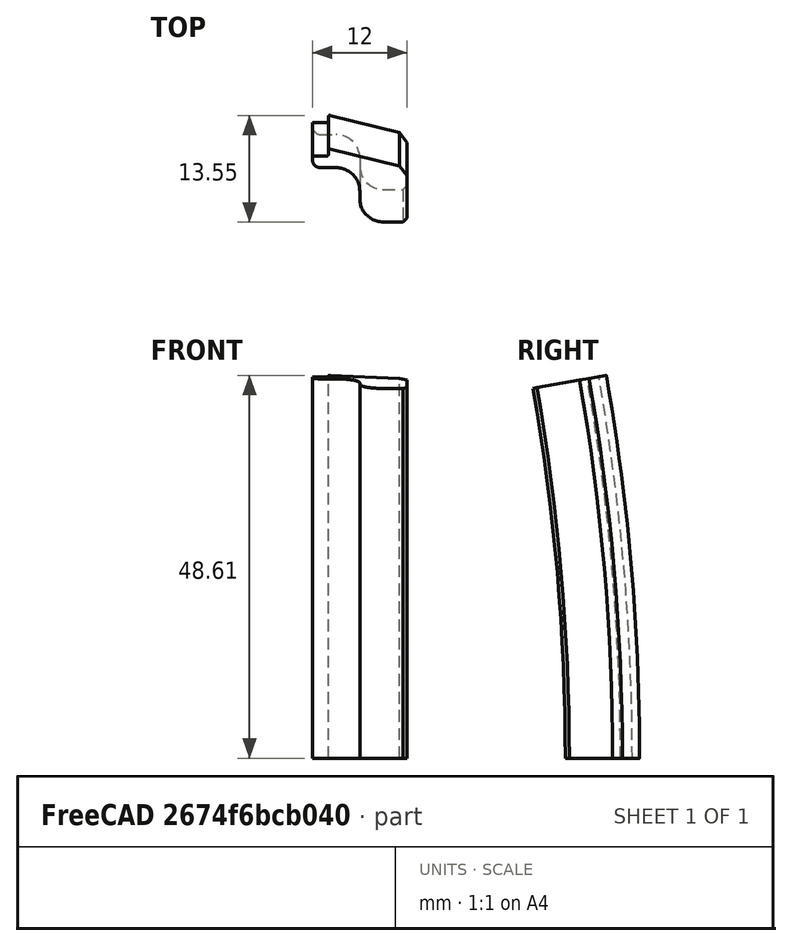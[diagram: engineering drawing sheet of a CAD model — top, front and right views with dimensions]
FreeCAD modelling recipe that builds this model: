
FCSTD DOCUMENT  (FreeCAD 0.16R)
Label: BeadLock3
License: All rights reserved
LicenseURL: http://en.wikipedia.org/wiki/All_rights_reserved
objects: PartDesign::Fillet×5, PartDesign::Chamfer×2, Sketcher::SketchObject×1, PartDesign::Revolution×1, Mesh::Feature×1
note: 10 computed .brp shape members not serialized (recipe doc carries the construction recipe); baked Part::Feature solids carry a one-line shape summary decoded from their .brp

FEATURE [Sketcher::SketchObject] Sketch
  sketch-geometry (8):
    g0: LineSegment StartX=0 StartY=279 StartZ=0 EndX=2 EndY=279 EndZ=0
    g1: LineSegment StartX=2 StartY=279 StartZ=0 EndX=2 EndY=280 EndZ=0
    g2: LineSegment StartX=0 StartY=277.5 StartZ=0 EndX=0 EndY=279 EndZ=0
    g3: LineSegment StartX=0 StartY=277.5 StartZ=0 EndX=6 EndY=277.5 EndZ=0
    g4: LineSegment StartX=6 StartY=277.5 StartZ=0 EndX=6 EndY=270.5 EndZ=0
    g5: LineSegment StartX=6 StartY=270.5 StartZ=0 EndX=12 EndY=270.5 EndZ=0
    g6: LineSegment StartX=12 StartY=270.5 StartZ=0 EndX=12 EndY=277.5 EndZ=0
    g7: LineSegment StartX=2 StartY=280 StartZ=0 EndX=12 EndY=277.5 EndZ=0
  constraints (24):
    c: Horizontal(g0)
    c: PointOnObject(g0,g-2)
    c: DistanceY(g0) = 279
    c: Distance(g0) = 2
    c: Coincident(g1,g0)
    c: Vertical(g1)
    c: Distance(g1) = 1
    c: Vertical(g2)
    c: Coincident(g2,g0)
    c: Distance(g2) = 1.5
    c: Horizontal(g3)
    c: Coincident(g3,g2)
    c: Distance(g3) = 6
    c: Vertical(g4)
    c: Coincident(g4,g3)
    c: Distance(g4) = 7
    c: Horizontal(g5)
    c: Coincident(g5,g4)
    c: Distance(g5) = 6
    c: Vertical(g6)
    c: Coincident(g5,g6)
    c: Distance(g6) = 7
    c: Coincident(g7,g1)
    c: Coincident(g7,g6)
FEATURE [PartDesign::Revolution] Revolution
  Angle = 10
  Axis = (1,0,0)
  Base = (0,0,0)
  ReferenceAxis = -> Sketch [H_Axis]
  Sketch = -> Sketch
FEATURE [PartDesign::Fillet] Fillet
  Base = -> Revolution [Edge17]
  Radius = 3
FEATURE [PartDesign::Fillet] Fillet001
  Base = -> Fillet [Edge23]
  Radius = 1
FEATURE [PartDesign::Fillet] Fillet002
  Base = -> Fillet001 [Edge26]
  Radius = 0.2
FEATURE [PartDesign::Fillet] Fillet003
  Base = -> Fillet002 [Edge13]
  Radius = 0.2
FEATURE [PartDesign::Chamfer] Chamfer
  Base = -> Fillet003 [Edge22]
  Size = 1
FEATURE [PartDesign::Chamfer] Chamfer001
  Base = -> Chamfer [Edge21]
  Size = 0.5
FEATURE [PartDesign::Fillet] Fillet004
  Base = -> Chamfer001 [Edge22]
  Radius = 3
FEATURE [Mesh::Feature] Mesh  label="Fillet004 (Meshed)"
